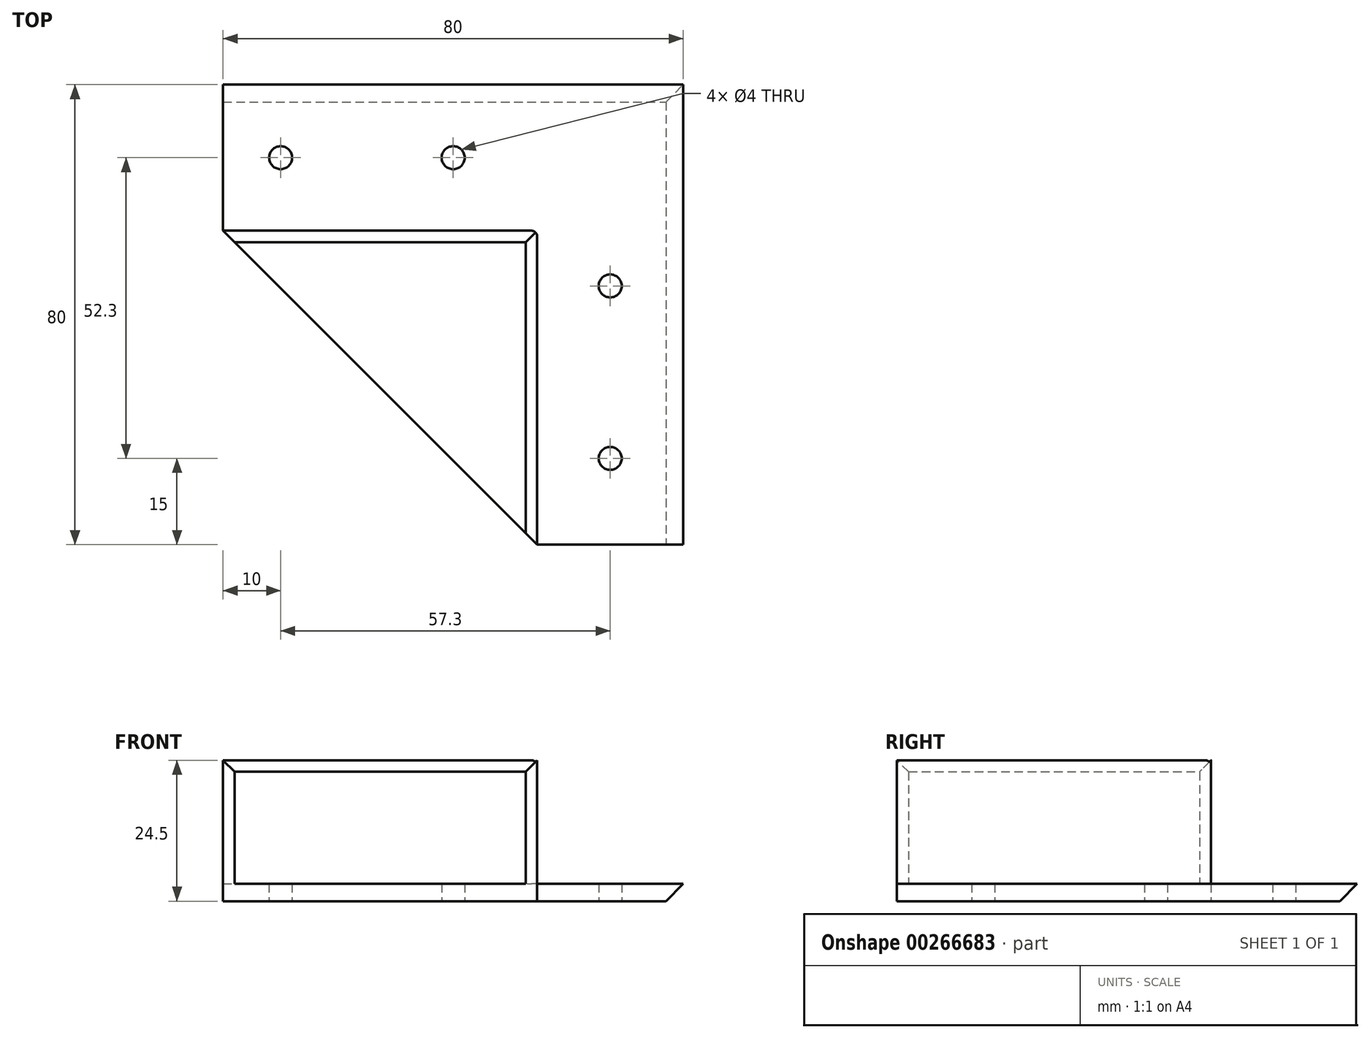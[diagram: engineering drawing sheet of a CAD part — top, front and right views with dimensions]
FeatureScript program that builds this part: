
annotation { "Feature Type Name" : "Feature", "Feature Type Description" : "" }
export const myFeature = defineFeature(function(context is Context, id is Id, definition is map)
    precondition{}
    {
        {
            var Q0;
            Q0=qCreatedBy(makeId("Top.planeOp"),FACE);
            var sketch = newSketch(context, id + "F0", { "sketchPlane" : qUnion([Q0])});
            skLineSegment(sketch, "E0", {"start": v(0, 0) * mm, "end": v(-80, 0) * mm});
            skLineSegment(sketch, "E1", {"start": v(-80, 0) * mm, "end": v(-80, -25.4) * mm});
            skLineSegment(sketch, "E2", {"start": v(-80, -25.4) * mm, "end": v(-25.4, -80) * mm});
            skLineSegment(sketch, "E3", {"start": v(-25.4, -80) * mm, "end": v(0, -80) * mm});
            skLineSegment(sketch, "E4", {"start": v(0, -80) * mm, "end": v(0, 0) * mm});
            skLineSegment(sketch, "E5", {"start": v(-80, -12.7) * mm, "end": v(0, -12.7) * mm, "construction": true});
            skLineSegment(sketch, "E6", {"start": v(-12.7, -80) * mm, "end": v(-12.7, 0) * mm, "construction": true});
            skCircle(sketch, "E7", {"center": v(-70, -12.7) * mm, "radius": 2 * mm});
            skCircle(sketch, "E8", {"center": v(-40, -12.7) * mm, "radius": 2 * mm});
            skCircle(sketch, "E9", {"center": v(-12.7, -35) * mm, "radius": 2 * mm});
            skCircle(sketch, "E10", {"center": v(-12.7, -65) * mm, "radius": 2 * mm});
            skSolve(sketch);
        }
        {
            var Q0;
            Q0=qSketchRegion(id+"F0",true);
            extrude(context, id + "F1", {"entities" : qUnion([Q0]), "depth" : 3 * mm});
        }
        {
            var Q0;
            Q0=makeQuery(id+"F1.opExtrude","CAP_FACE",FACE,{"disambiguationData":[OSD([sQuery(id+"F0.wireOp",EDGE,"E0"),sQuery(id+"F0.wireOp",EDGE,"E1"),sQuery(id+"F0.wireOp",EDGE,"E2"),sQuery(id+"F0.wireOp",EDGE,"E3"),sQuery(id+"F0.wireOp",EDGE,"E4"),sQuery(id+"F0.wireOp",EDGE,"E7"),sQuery(id+"F0.wireOp",EDGE,"E8"),sQuery(id+"F0.wireOp",EDGE,"E9"),sQuery(id+"F0.wireOp",EDGE,"E10")])],"isStart":false});
            var sketch = newSketch(context, id + "F2", { "sketchPlane" : qUnion([Q0])});
            skLineSegment(sketch, "E11", {"start": v(-80, -25.4) * mm, "end": v(-25.4, -25.4) * mm});
            skLineSegment(sketch, "E12", {"start": v(-25.4, -25.4) * mm, "end": v(-25.4, -80) * mm});
            skLineSegment(sketch, "E13", {"start": v(-25.4, -80) * mm, "end": v(-27.4, -78) * mm});
            skLineSegment(sketch, "E14", {"start": v(-27.4, -78) * mm, "end": v(-27.4, -27.4) * mm});
            skLineSegment(sketch, "E15", {"start": v(-27.4, -27.4) * mm, "end": v(-78, -27.4) * mm});
            skLineSegment(sketch, "E16", {"start": v(-78, -27.4) * mm, "end": v(-80, -25.4) * mm});
            skSolve(sketch);
        }
        {
            var Q0;
            Q0=qSketchRegion(id+"F2",true);
            extrude(context, id + "F3", {"entities" : qUnion([Q0]), "operationType" : NewBodyOperationType.ADD, "depth" : 21.5 * mm});
        }
        {
            var Q0;
            Q0=makeQuery(id+"F1.opExtrude","CAP_EDGE",EDGE,{"disambiguationData":[OSD([sQuery(id+"F0.wireOp",EDGE,"E0")])],"isStart":true});
            var Q1;
            Q1=makeQuery(id+"F1.opExtrude","CAP_EDGE",EDGE,{"disambiguationData":[OSD([sQuery(id+"F0.wireOp",EDGE,"E4")])],"isStart":true});
            chamfer(context, id + "F4", {"entities" : qUnion([Q0, Q1]), "width" : 3 * mm, "tangentPropagation" : true});
        }
        {
            var Q0;
            Q0=makeQuery(id+"F3.opExtrude","SWEPT_EDGE",EDGE,{"disambiguationData":[OSD([sQuery(id+"F2.wireOp",EDGE,"E11"),sQuery(id+"F2.wireOp",EDGE,"E12")])]});
            fillet(context, id + "F5", {"entities" : qUnion([Q0]), "radius" : 1 * mm, "tangentPropagation" : true, "allowEdgeOverflow" : false});
        }
        {
            var Q0;
            Q0=makeQuery(id+"F3.opExtrude","CAP_EDGE",EDGE,{"disambiguationData":[OSD([sQuery(id+"F2.wireOp",EDGE,"E15")])],"isStart":false});
            var Q1;
            Q1=makeQuery(id+"F3.opExtrude","CAP_EDGE",EDGE,{"disambiguationData":[OSD([sQuery(id+"F2.wireOp",EDGE,"E14")])],"isStart":false});
            chamfer(context, id + "F6", {"entities" : qUnion([Q0, Q1]), "width" : 2 * mm, "tangentPropagation" : true});
        }
    });
